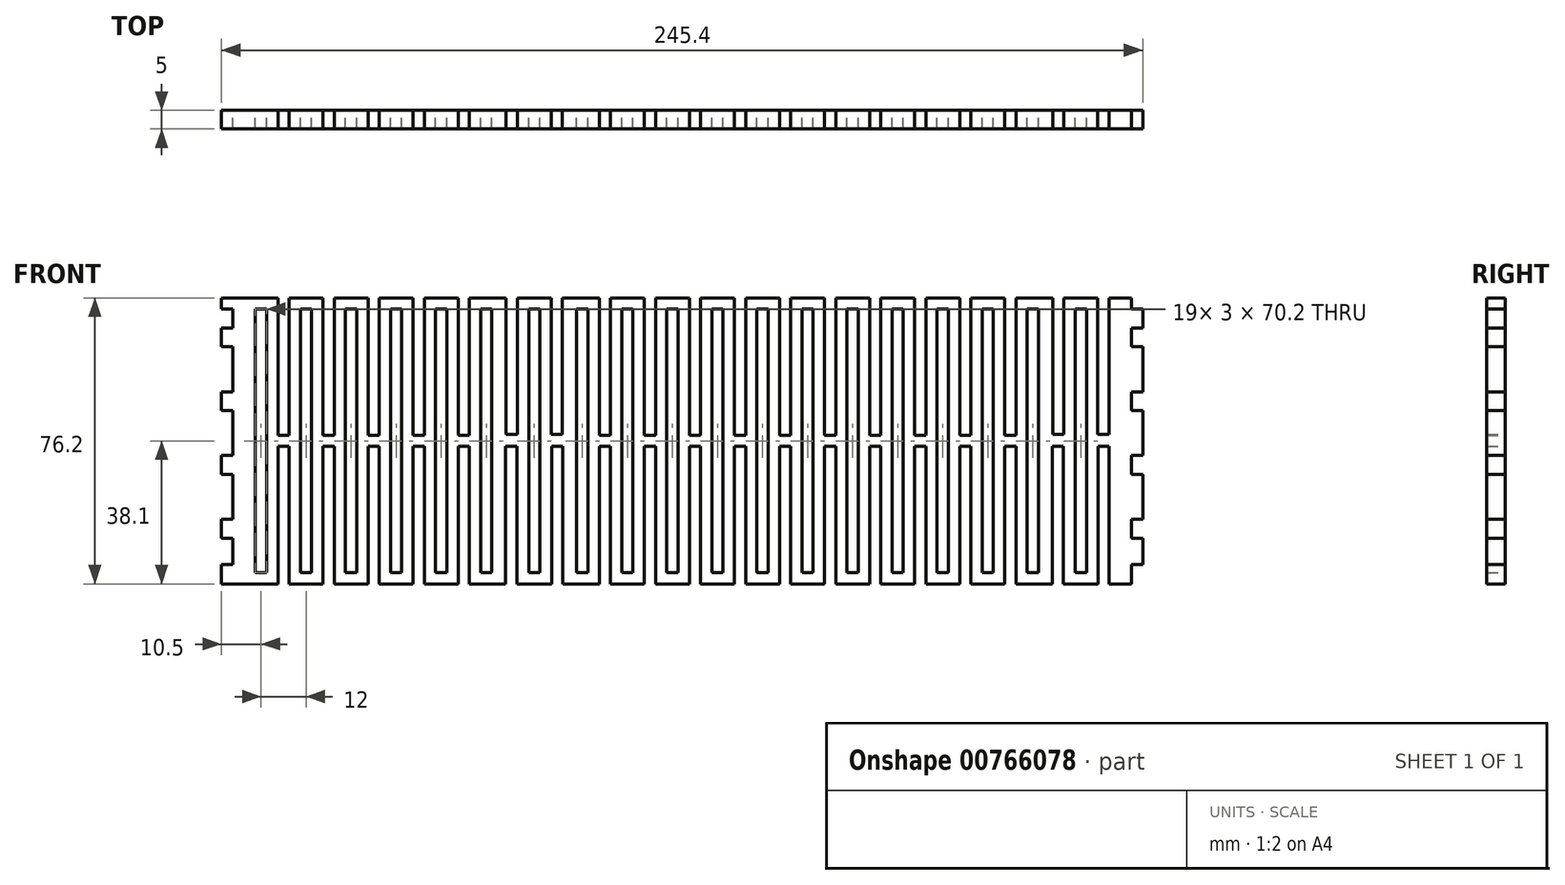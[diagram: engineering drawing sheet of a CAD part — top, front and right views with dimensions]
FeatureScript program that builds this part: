
annotation { "Feature Type Name" : "Feature", "Feature Type Description" : "" }
export const myFeature = defineFeature(function(context is Context, id is Id, definition is map)
    precondition{}
    {
        {
            var Q0;
            Q0=qCreatedBy(makeId("Front.planeOp"),FACE);
            var sketch = newSketch(context, id + "F0", { "sketchPlane" : qUnion([Q0])});
            skLineSegment(sketch, "E0.bottom", {"start": v(0, 0) * mm, "end": v(15, 0) * mm});
            skLineSegment(sketch, "E0.top", {"start": v(0, 76.2) * mm, "end": v(15, 76.2) * mm});
            skLineSegment(sketch, "E0.left", {"start": v(0, 0) * mm, "end": v(0, 5.2) * mm});
            skLineSegment(sketch, "E1.bottom", {"start": v(9, 73.2) * mm, "end": v(12, 73.2) * mm});
            skLineSegment(sketch, "E1.top", {"start": v(9, 3) * mm, "end": v(12, 3) * mm});
            skLineSegment(sketch, "E1.left", {"start": v(9, 73.2) * mm, "end": v(9, 3) * mm});
            skLineSegment(sketch, "E1.right", {"start": v(12, 73.2) * mm, "end": v(12, 3) * mm});
            skLineSegment(sketch, "E2.left", {"start": v(15, 76.2) * mm, "end": v(15, 39.6) * mm});
            skLineSegment(sketch, "E2.right", {"start": v(18, 76.2) * mm, "end": v(18, 39.6) * mm});
            skLineSegment(sketch, "E3.bottom", {"start": v(15, 36.6) * mm, "end": v(18, 36.6) * mm});
            skLineSegment(sketch, "E3.left", {"start": v(15, 36.6) * mm, "end": v(15, 0) * mm});
            skLineSegment(sketch, "E3.right", {"start": v(18, 36.6) * mm, "end": v(18, 0) * mm});
            skPoint(sketch, "E4.endSnap0", {"position": v(6, 38.1) * mm});
            skLineSegment(sketch, "E5", {"start": v(15, 39.6) * mm, "end": v(18, 39.6) * mm});
            skLineSegment(sketch, "E6.bottom", {"start": v(21, 3) * mm, "end": v(22.5, 3) * mm});
            skLineSegment(sketch, "E6.top", {"start": v(21, 73.2) * mm, "end": v(22.5, 73.2) * mm});
            skLineSegment(sketch, "E6.left", {"start": v(21, 3) * mm, "end": v(21, 73.2) * mm});
            skLineSegment(sketch, "E7.MirrorCS", {"start": v(24, 3) * mm, "end": v(24, 73.2) * mm});
            skLineSegment(sketch, "E8.MirrorCS", {"start": v(27, 76.2) * mm, "end": v(27, 39.6) * mm});
            skLineSegment(sketch, "E9.MirrorCS", {"start": v(30, 76.2) * mm, "end": v(30, 39.6) * mm});
            skLineSegment(sketch, "E10.MirrorCS", {"start": v(30, 39.6) * mm, "end": v(27, 39.6) * mm});
            skLineSegment(sketch, "E11.MirrorCS", {"start": v(30, 36.6) * mm, "end": v(27, 36.6) * mm});
            skLineSegment(sketch, "E12.MirrorCS", {"start": v(27, 36.6) * mm, "end": v(27, 0) * mm});
            skLineSegment(sketch, "E13.MirrorCS", {"start": v(30, 36.6) * mm, "end": v(30, 0) * mm});
            skLineSegment(sketch, "E14.MirrorCS", {"start": v(33, 73.2) * mm, "end": v(33, 3) * mm});
            skLineSegment(sketch, "E15.MirrorCS", {"start": v(36, 73.2) * mm, "end": v(33, 73.2) * mm});
            skLineSegment(sketch, "E16.MirrorCS", {"start": v(36, 73.2) * mm, "end": v(36, 3) * mm});
            skLineSegment(sketch, "E17.MirrorCS", {"start": v(36, 3) * mm, "end": v(33, 3) * mm});
            skLineSegment(sketch, "E18.MirrorCS", {"start": v(24, 3) * mm, "end": v(22.5, 3) * mm});
            skLineSegment(sketch, "E19", {"start": v(22.5, 73.2) * mm, "end": v(24, 73.2) * mm});
            skLineSegment(sketch, "E20.trimOffspring", {"start": v(18, 76.2) * mm, "end": v(27, 76.2) * mm});
            skLineSegment(sketch, "E21.trimOffspring", {"start": v(30, 76.2) * mm, "end": v(39, 76.2) * mm});
            skLineSegment(sketch, "E22.trimOffspring", {"start": v(30, 0) * mm, "end": v(39, 0) * mm});
            skLineSegment(sketch, "E23.trimOffspring", {"start": v(18, 0) * mm, "end": v(27, 0) * mm});
            skLineSegment(sketch, "E24", {"start": v(39, 76.2) * mm, "end": v(39, 39.6) * mm});
            skLineSegment(sketch, "E25", {"start": v(39, 39.6) * mm, "end": v(40.5, 39.6) * mm});
            skLineSegment(sketch, "E26.bottom", {"start": v(39, 36.6) * mm, "end": v(40.5, 36.6) * mm});
            skLineSegment(sketch, "E26.left", {"start": v(39, 36.6) * mm, "end": v(39, 3) * mm});
            skLineSegment(sketch, "E27.MirrorCS", {"start": v(42, 76.2) * mm, "end": v(42, 39.6) * mm});
            skLineSegment(sketch, "E28.MirrorCS", {"start": v(45, 73.2) * mm, "end": v(45, 3) * mm});
            skLineSegment(sketch, "E29.MirrorCS", {"start": v(48, 73.2) * mm, "end": v(48, 3) * mm});
            skLineSegment(sketch, "E30.MirrorCS", {"start": v(51, 76.2) * mm, "end": v(51, 39.6) * mm});
            skLineSegment(sketch, "E31.MirrorCS", {"start": v(54, 76.2) * mm, "end": v(54, 39.6) * mm});
            skLineSegment(sketch, "E32.MirrorCS", {"start": v(57, 3) * mm, "end": v(57, 73.2) * mm});
            skLineSegment(sketch, "E33.MirrorCS", {"start": v(60, 3) * mm, "end": v(60, 73.2) * mm});
            skLineSegment(sketch, "E34.MirrorCS", {"start": v(63, 76.2) * mm, "end": v(63, 39.6) * mm});
            skLineSegment(sketch, "E35.MirrorCS", {"start": v(66, 76.2) * mm, "end": v(66, 39.6) * mm});
            skLineSegment(sketch, "E36.MirrorCS", {"start": v(69, 73.2) * mm, "end": v(69, 3) * mm});
            skLineSegment(sketch, "E37.MirrorCS", {"start": v(51, 36.6) * mm, "end": v(51, 0) * mm});
            skLineSegment(sketch, "E38.MirrorCS", {"start": v(54, 36.6) * mm, "end": v(54, 0) * mm});
            skLineSegment(sketch, "E39.MirrorCS", {"start": v(63, 36.6) * mm, "end": v(63, 0) * mm});
            skLineSegment(sketch, "E40.MirrorCS", {"start": v(66, 36.6) * mm, "end": v(66, 0) * mm});
            skLineSegment(sketch, "E41.MirrorCS", {"start": v(72, 73.2) * mm, "end": v(72, 3) * mm});
            skLineSegment(sketch, "E42.MirrorCS", {"start": v(42, 36.6) * mm, "end": v(42, 3) * mm});
            skLineSegment(sketch, "E43.MirrorCS", {"start": v(45, 3) * mm, "end": v(48, 3) * mm});
            skLineSegment(sketch, "E44.MirrorCS", {"start": v(57, 3) * mm, "end": v(58.5, 3) * mm});
            skLineSegment(sketch, "E45.MirrorCS", {"start": v(60, 3) * mm, "end": v(58.5, 3) * mm});
            skLineSegment(sketch, "E46.MirrorCS", {"start": v(72, 3) * mm, "end": v(69, 3) * mm});
            skLineSegment(sketch, "E47.MirrorCS", {"start": v(51, 36.6) * mm, "end": v(54, 36.6) * mm});
            skLineSegment(sketch, "E48.MirrorCS", {"start": v(66, 39.6) * mm, "end": v(63, 39.6) * mm});
            skLineSegment(sketch, "E49.MirrorCS", {"start": v(51, 39.6) * mm, "end": v(54, 39.6) * mm});
            skLineSegment(sketch, "E50.MirrorCS", {"start": v(66, 36.6) * mm, "end": v(63, 36.6) * mm});
            skLineSegment(sketch, "E51.MirrorCS", {"start": v(42, 36.6) * mm, "end": v(40.5, 36.6) * mm});
            skLineSegment(sketch, "E52.MirrorCS", {"start": v(45, 73.2) * mm, "end": v(48, 73.2) * mm});
            skLineSegment(sketch, "E53.MirrorCS", {"start": v(58.5, 73.2) * mm, "end": v(57, 73.2) * mm});
            skLineSegment(sketch, "E54.MirrorCS", {"start": v(60, 73.2) * mm, "end": v(58.5, 73.2) * mm});
            skLineSegment(sketch, "E55.MirrorCS", {"start": v(72, 73.2) * mm, "end": v(69, 73.2) * mm});
            skLineSegment(sketch, "E56.trimOffspring", {"start": v(42, 76.2) * mm, "end": v(51, 76.2) * mm});
            skLineSegment(sketch, "E57", {"start": v(40.5, 39.6) * mm, "end": v(42, 39.6) * mm});
            skLineSegment(sketch, "E58", {"start": v(39, 3) * mm, "end": v(39, 0) * mm});
            skLineSegment(sketch, "E59", {"start": v(42, 0) * mm, "end": v(42, 3) * mm});
            skLineSegment(sketch, "E60.trimOffspring", {"start": v(42, 0) * mm, "end": v(51, 0) * mm});
            skLineSegment(sketch, "E61.trimOffspring", {"start": v(54, 0) * mm, "end": v(63, 0) * mm});
            skLineSegment(sketch, "E62.trimOffspring", {"start": v(66, 0) * mm, "end": v(75.68, 0) * mm});
            skLineSegment(sketch, "E63.trimOffspring", {"start": v(54, 76.2) * mm, "end": v(63, 76.2) * mm});
            skLineSegment(sketch, "E64.trimOffspring", {"start": v(66, 76.2) * mm, "end": v(75.8, 76.2) * mm});
            skLineSegment(sketch, "E65.top", {"start": v(75.8, 39.81) * mm, "end": v(78.8, 39.81) * mm});
            skLineSegment(sketch, "E65.left", {"start": v(75.8, 76.2) * mm, "end": v(75.8, 39.81) * mm});
            skLineSegment(sketch, "E65.right", {"start": v(78.8, 76.2) * mm, "end": v(78.8, 39.81) * mm});
            skLineSegment(sketch, "E66.bottom", {"start": v(75.68, 36.6) * mm, "end": v(78.66, 36.6) * mm});
            skLineSegment(sketch, "E66.left", {"start": v(75.68, 36.6) * mm, "end": v(75.68, 0) * mm});
            skLineSegment(sketch, "E66.right", {"start": v(78.66, 36.6) * mm, "end": v(78.66, 0) * mm});
            skLineSegment(sketch, "E67.bottom", {"start": v(81.8, 73.2) * mm, "end": v(83.3, 73.2) * mm});
            skLineSegment(sketch, "E67.top", {"start": v(81.8, 3) * mm, "end": v(83.3, 3) * mm});
            skLineSegment(sketch, "E67.left", {"start": v(81.8, 73.2) * mm, "end": v(81.8, 3) * mm});
            skPoint(sketch, "E68.orphan", {"position": v(73.83, 73.2) * mm});
            skLineSegment(sketch, "E69.MirrorCS", {"start": v(84.8, 73.2) * mm, "end": v(84.8, 3) * mm});
            skLineSegment(sketch, "E70.MirrorCS", {"start": v(87.8, 76.2) * mm, "end": v(87.8, 39.81) * mm});
            skLineSegment(sketch, "E71.MirrorCS", {"start": v(90.8, 76.2) * mm, "end": v(90.8, 39.81) * mm});
            skLineSegment(sketch, "E72.MirrorCS", {"start": v(94.6, 73.2) * mm, "end": v(94.6, 3) * mm});
            skLineSegment(sketch, "E73.MirrorCS", {"start": v(97.6, 73.2) * mm, "end": v(97.6, 3) * mm});
            skLineSegment(sketch, "E74.MirrorCS", {"start": v(100.6, 76.2) * mm, "end": v(100.6, 39.6) * mm});
            skLineSegment(sketch, "E75.MirrorCS", {"start": v(103.6, 76.2) * mm, "end": v(103.6, 39.6) * mm});
            skLineSegment(sketch, "E76.MirrorCS", {"start": v(106.6, 3) * mm, "end": v(106.6, 73.2) * mm});
            skLineSegment(sketch, "E77.MirrorCS", {"start": v(109.6, 3) * mm, "end": v(109.6, 73.2) * mm});
            skLineSegment(sketch, "E78.MirrorCS", {"start": v(112.6, 76.2) * mm, "end": v(112.6, 39.6) * mm});
            skLineSegment(sketch, "E79.MirrorCS", {"start": v(115.6, 76.2) * mm, "end": v(115.6, 39.6) * mm});
            skLineSegment(sketch, "E80.MirrorCS", {"start": v(118.6, 73.2) * mm, "end": v(118.6, 3) * mm});
            skLineSegment(sketch, "E81.MirrorCS", {"start": v(121.6, 73.2) * mm, "end": v(121.6, 3) * mm});
            skLineSegment(sketch, "E82.MirrorCS", {"start": v(124.6, 76.2) * mm, "end": v(124.6, 39.6) * mm});
            skLineSegment(sketch, "E83.MirrorCS", {"start": v(127.6, 76.2) * mm, "end": v(127.6, 39.6) * mm});
            skLineSegment(sketch, "E84.MirrorCS", {"start": v(130.6, 73.2) * mm, "end": v(130.6, 3) * mm});
            skLineSegment(sketch, "E85.MirrorCS", {"start": v(133.6, 73.2) * mm, "end": v(133.6, 3) * mm});
            skLineSegment(sketch, "E86.MirrorCS", {"start": v(136.6, 76.2) * mm, "end": v(136.6, 39.6) * mm});
            skLineSegment(sketch, "E87.MirrorCS", {"start": v(139.6, 76.2) * mm, "end": v(139.6, 39.6) * mm});
            skLineSegment(sketch, "E88.MirrorCS", {"start": v(142.6, 3) * mm, "end": v(142.6, 73.2) * mm});
            skLineSegment(sketch, "E89.MirrorCS", {"start": v(148.6, 76.2) * mm, "end": v(148.6, 39.6) * mm});
            skLineSegment(sketch, "E90.MirrorCS", {"start": v(151.6, 76.2) * mm, "end": v(151.6, 39.6) * mm});
            skLineSegment(sketch, "E91.MirrorCS", {"start": v(94.6, 73.2) * mm, "end": v(97.6, 73.2) * mm});
            skLineSegment(sketch, "E92.MirrorCS", {"start": v(84.8, 73.2) * mm, "end": v(83.3, 73.2) * mm});
            skLineSegment(sketch, "E93.MirrorCS", {"start": v(121.6, 73.2) * mm, "end": v(118.6, 73.2) * mm});
            skLineSegment(sketch, "E94.MirrorCS", {"start": v(108.1, 73.2) * mm, "end": v(109.6, 73.2) * mm});
            skLineSegment(sketch, "E95.MirrorCS", {"start": v(106.6, 73.2) * mm, "end": v(108.1, 73.2) * mm});
            skLineSegment(sketch, "E96.MirrorCS", {"start": v(130.6, 73.2) * mm, "end": v(133.6, 73.2) * mm});
            skLineSegment(sketch, "E97.MirrorCS", {"start": v(144.1, 73.2) * mm, "end": v(142.6, 73.2) * mm});
            skLineSegment(sketch, "E98.MirrorCS", {"start": v(145.6, 73.2) * mm, "end": v(144.1, 73.2) * mm});
            skLineSegment(sketch, "E99.MirrorCS", {"start": v(156.1, 73.2) * mm, "end": v(154.6, 73.2) * mm});
            skLineSegment(sketch, "E100.MirrorCS", {"start": v(90.8, 39.81) * mm, "end": v(87.8, 39.81) * mm});
            skLineSegment(sketch, "E101.MirrorCS", {"start": v(100.6, 39.6) * mm, "end": v(103.6, 39.6) * mm});
            skLineSegment(sketch, "E102.MirrorCS", {"start": v(115.6, 39.6) * mm, "end": v(112.6, 39.6) * mm});
            skLineSegment(sketch, "E103.MirrorCS", {"start": v(126.1, 39.6) * mm, "end": v(124.6, 39.6) * mm});
            skLineSegment(sketch, "E104.MirrorCS", {"start": v(127.6, 39.6) * mm, "end": v(126.1, 39.6) * mm});
            skLineSegment(sketch, "E105.MirrorCS", {"start": v(136.6, 39.6) * mm, "end": v(139.6, 39.6) * mm});
            skLineSegment(sketch, "E106.MirrorCS", {"start": v(151.6, 39.6) * mm, "end": v(148.6, 39.6) * mm});
            skLineSegment(sketch, "E107.MirrorCS", {"start": v(151.6, 36.6) * mm, "end": v(148.6, 36.6) * mm});
            skLineSegment(sketch, "E108.MirrorCS", {"start": v(136.6, 36.6) * mm, "end": v(139.6, 36.6) * mm});
            skLineSegment(sketch, "E109.MirrorCS", {"start": v(124.6, 36.6) * mm, "end": v(126.1, 36.6) * mm});
            skLineSegment(sketch, "E110.MirrorCS", {"start": v(115.6, 36.6) * mm, "end": v(112.6, 36.6) * mm});
            skLineSegment(sketch, "E111.MirrorCS", {"start": v(100.6, 36.6) * mm, "end": v(103.6, 36.6) * mm});
            skLineSegment(sketch, "E112.MirrorCS", {"start": v(87.94, 36.6) * mm, "end": v(87.94, 0) * mm});
            skLineSegment(sketch, "E113.MirrorCS", {"start": v(90.92, 36.6) * mm, "end": v(90.92, 0) * mm});
            skLineSegment(sketch, "E114.MirrorCS", {"start": v(100.6, 36.6) * mm, "end": v(100.6, 0) * mm});
            skLineSegment(sketch, "E115.MirrorCS", {"start": v(103.6, 36.6) * mm, "end": v(103.6, 0) * mm});
            skLineSegment(sketch, "E116.MirrorCS", {"start": v(112.6, 36.6) * mm, "end": v(112.6, 0) * mm});
            skLineSegment(sketch, "E117.MirrorCS", {"start": v(115.6, 36.6) * mm, "end": v(115.6, 0) * mm});
            skLineSegment(sketch, "E118.MirrorCS", {"start": v(124.6, 36.6) * mm, "end": v(124.6, 3) * mm});
            skLineSegment(sketch, "E119.MirrorCS", {"start": v(127.6, 36.6) * mm, "end": v(127.6, 3) * mm});
            skLineSegment(sketch, "E120.MirrorCS", {"start": v(124.6, 0) * mm, "end": v(124.6, 3) * mm});
            skLineSegment(sketch, "E121.MirrorCS", {"start": v(127.6, 3) * mm, "end": v(127.6, 0) * mm});
            skLineSegment(sketch, "E122.MirrorCS", {"start": v(136.6, 36.6) * mm, "end": v(136.6, 0) * mm});
            skLineSegment(sketch, "E123.MirrorCS", {"start": v(139.6, 36.6) * mm, "end": v(139.6, 0) * mm});
            skLineSegment(sketch, "E124.MirrorCS", {"start": v(84.8, 3) * mm, "end": v(83.3, 3) * mm});
            skLineSegment(sketch, "E125.MirrorCS", {"start": v(94.6, 3) * mm, "end": v(97.6, 3) * mm});
            skLineSegment(sketch, "E126.MirrorCS", {"start": v(106.6, 3) * mm, "end": v(108.1, 3) * mm});
            skLineSegment(sketch, "E127.MirrorCS", {"start": v(109.6, 3) * mm, "end": v(108.1, 3) * mm});
            skLineSegment(sketch, "E128.MirrorCS", {"start": v(121.6, 3) * mm, "end": v(118.6, 3) * mm});
            skLineSegment(sketch, "E129.MirrorCS", {"start": v(130.6, 3) * mm, "end": v(133.6, 3) * mm});
            skLineSegment(sketch, "E130.MirrorCS", {"start": v(142.6, 3) * mm, "end": v(144.1, 3) * mm});
            skLineSegment(sketch, "E131.MirrorCS", {"start": v(154.6, 73.2) * mm, "end": v(154.6, 3) * mm});
            skLineSegment(sketch, "E132.MirrorCS", {"start": v(145.6, 3) * mm, "end": v(145.6, 73.2) * mm});
            skLineSegment(sketch, "E133.MirrorCS", {"start": v(151.6, 36.6) * mm, "end": v(151.6, 0) * mm});
            skLineSegment(sketch, "E134.MirrorCS", {"start": v(148.6, 36.6) * mm, "end": v(148.6, 0) * mm});
            skLineSegment(sketch, "E135.trimOffspring", {"start": v(103.6, 76.2) * mm, "end": v(112.6, 76.2) * mm});
            skLineSegment(sketch, "E136.trimOffspring", {"start": v(90.8, 76.2) * mm, "end": v(100.6, 76.2) * mm});
            skLineSegment(sketch, "E137.trimOffspring", {"start": v(115.6, 76.2) * mm, "end": v(124.6, 76.2) * mm});
            skLineSegment(sketch, "E138.trimOffspring", {"start": v(127.6, 76.2) * mm, "end": v(136.6, 76.2) * mm});
            skLineSegment(sketch, "E139.trimOffspring", {"start": v(139.6, 76.2) * mm, "end": v(148.6, 76.2) * mm});
            skLineSegment(sketch, "E140.trimOffspring", {"start": v(151.6, 76.2) * mm, "end": v(160.6, 76.2) * mm});
            skLineSegment(sketch, "E141.trimOffspring", {"start": v(151.6, 0) * mm, "end": v(160.6, 0) * mm});
            skLineSegment(sketch, "E142.trimOffspring", {"start": v(139.6, 0) * mm, "end": v(148.6, 0) * mm});
            skLineSegment(sketch, "E143.trimOffspring", {"start": v(127.6, 0) * mm, "end": v(136.6, 0) * mm});
            skLineSegment(sketch, "E144.trimOffspring", {"start": v(115.6, 0) * mm, "end": v(124.6, 0) * mm});
            skLineSegment(sketch, "E145.trimOffspring", {"start": v(103.6, 0) * mm, "end": v(112.6, 0) * mm});
            skLineSegment(sketch, "E146.trimOffspring", {"start": v(90.92, 0) * mm, "end": v(100.6, 0) * mm});
            skLineSegment(sketch, "E147", {"start": v(144.1, 3) * mm, "end": v(145.6, 3) * mm});
            skLineSegment(sketch, "E148", {"start": v(154.6, 3) * mm, "end": v(156.1, 3) * mm});
            skLineSegment(sketch, "E149", {"start": v(87.94, 36.6) * mm, "end": v(90.92, 36.6) * mm});
            skLineSegment(sketch, "E150", {"start": v(126.1, 36.6) * mm, "end": v(127.6, 36.6) * mm});
            skPoint(sketch, "E151.end.orphan", {"position": v(157.6, 0) * mm});
            skPoint(sketch, "E152.orphan", {"position": v(157.6, 3) * mm});
            skLineSegment(sketch, "E153.MirrorCS", {"start": v(157.6, 73.2) * mm, "end": v(157.6, 3) * mm});
            skLineSegment(sketch, "E154.MirrorCS", {"start": v(160.6, 76.2) * mm, "end": v(160.6, 39.6) * mm});
            skLineSegment(sketch, "E155.MirrorCS", {"start": v(163.6, 76.2) * mm, "end": v(163.6, 39.6) * mm});
            skLineSegment(sketch, "E156.MirrorCS", {"start": v(166.6, 3) * mm, "end": v(166.6, 73.2) * mm});
            skLineSegment(sketch, "E157.MirrorCS", {"start": v(169.6, 3) * mm, "end": v(169.6, 73.2) * mm});
            skLineSegment(sketch, "E158.MirrorCS", {"start": v(172.6, 76.2) * mm, "end": v(172.6, 39.6) * mm});
            skLineSegment(sketch, "E159.MirrorCS", {"start": v(175.6, 76.2) * mm, "end": v(175.6, 39.6) * mm});
            skLineSegment(sketch, "E160.MirrorCS", {"start": v(178.6, 73.2) * mm, "end": v(178.6, 3) * mm});
            skLineSegment(sketch, "E161.MirrorCS", {"start": v(181.6, 73.2) * mm, "end": v(181.6, 3) * mm});
            skLineSegment(sketch, "E162.MirrorCS", {"start": v(184.6, 76.2) * mm, "end": v(184.6, 39.6) * mm});
            skLineSegment(sketch, "E163.MirrorCS", {"start": v(187.6, 76.2) * mm, "end": v(187.6, 39.6) * mm});
            skLineSegment(sketch, "E164.MirrorCS", {"start": v(190.6, 73.2) * mm, "end": v(190.6, 3) * mm});
            skLineSegment(sketch, "E165.MirrorCS", {"start": v(193.6, 73.2) * mm, "end": v(193.6, 3) * mm});
            skLineSegment(sketch, "E166.MirrorCS", {"start": v(190.6, 73.2) * mm, "end": v(193.6, 73.2) * mm});
            skLineSegment(sketch, "E167.MirrorCS", {"start": v(199.6, 76.2) * mm, "end": v(199.6, 39.6) * mm});
            skLineSegment(sketch, "E168.MirrorCS", {"start": v(202.6, 3) * mm, "end": v(202.6, 73.2) * mm});
            skLineSegment(sketch, "E169.MirrorCS", {"start": v(205.6, 3) * mm, "end": v(205.6, 73.2) * mm});
            skLineSegment(sketch, "E170.MirrorCS", {"start": v(208.6, 76.2) * mm, "end": v(208.6, 39.6) * mm});
            skLineSegment(sketch, "E171.MirrorCS", {"start": v(211.6, 76.2) * mm, "end": v(211.6, 39.6) * mm});
            skLineSegment(sketch, "E172.MirrorCS", {"start": v(214.6, 73.2) * mm, "end": v(214.6, 3) * mm});
            skLineSegment(sketch, "E173.MirrorCS", {"start": v(217.6, 73.2) * mm, "end": v(217.6, 3) * mm});
            skLineSegment(sketch, "E174.MirrorCS", {"start": v(157.6, 3) * mm, "end": v(156.1, 3) * mm});
            skLineSegment(sketch, "E175.MirrorCS", {"start": v(168.1, 3) * mm, "end": v(166.6, 3) * mm});
            skLineSegment(sketch, "E176.MirrorCS", {"start": v(169.6, 3) * mm, "end": v(168.1, 3) * mm});
            skLineSegment(sketch, "E177.MirrorCS", {"start": v(172.6, 36.6) * mm, "end": v(172.6, 0) * mm});
            skLineSegment(sketch, "E178.MirrorCS", {"start": v(175.6, 36.6) * mm, "end": v(175.6, 0) * mm});
            skLineSegment(sketch, "E179.MirrorCS", {"start": v(181.6, 3) * mm, "end": v(178.6, 3) * mm});
            skLineSegment(sketch, "E180.MirrorCS", {"start": v(184.6, 0) * mm, "end": v(175.6, 0) * mm});
            skLineSegment(sketch, "E181.MirrorCS", {"start": v(190.6, 3) * mm, "end": v(193.6, 3) * mm});
            skLineSegment(sketch, "E182.MirrorCS", {"start": v(184.6, 36.6) * mm, "end": v(184.6, 3) * mm});
            skLineSegment(sketch, "E183.MirrorCS", {"start": v(187.6, 36.6) * mm, "end": v(187.6, 3) * mm});
            skLineSegment(sketch, "E184.MirrorCS", {"start": v(187.6, 0) * mm, "end": v(187.6, 3) * mm});
            skLineSegment(sketch, "E185.MirrorCS", {"start": v(184.6, 3) * mm, "end": v(184.6, 0) * mm});
            skLineSegment(sketch, "E186.MirrorCS", {"start": v(196.6, 36.6) * mm, "end": v(196.6, 0) * mm});
            skLineSegment(sketch, "E187.MirrorCS", {"start": v(199.6, 36.6) * mm, "end": v(199.6, 0) * mm});
            skLineSegment(sketch, "E188.MirrorCS", {"start": v(202.6, 3) * mm, "end": v(204.1, 3) * mm});
            skLineSegment(sketch, "E189.MirrorCS", {"start": v(205.6, 3) * mm, "end": v(204.1, 3) * mm});
            skLineSegment(sketch, "E190.MirrorCS", {"start": v(217.6, 3) * mm, "end": v(214.6, 3) * mm});
            skLineSegment(sketch, "E191.MirrorCS", {"start": v(211.6, 36.6) * mm, "end": v(211.6, 0) * mm});
            skLineSegment(sketch, "E192.MirrorCS", {"start": v(221.28, 36.6) * mm, "end": v(221.28, 0) * mm});
            skLineSegment(sketch, "E193.MirrorCS", {"start": v(227.4, 73.2) * mm, "end": v(227.4, 3) * mm});
            skLineSegment(sketch, "E194.MirrorCS", {"start": v(160.6, 36.6) * mm, "end": v(160.6, 0) * mm});
            skLineSegment(sketch, "E195.MirrorCS", {"start": v(175.6, 39.6) * mm, "end": v(172.6, 39.6) * mm});
            skLineSegment(sketch, "E196.MirrorCS", {"start": v(184.6, 39.6) * mm, "end": v(186.1, 39.6) * mm});
            skLineSegment(sketch, "E197.MirrorCS", {"start": v(186.1, 39.6) * mm, "end": v(187.6, 39.6) * mm});
            skLineSegment(sketch, "E198.MirrorCS", {"start": v(196.6, 39.6) * mm, "end": v(199.6, 39.6) * mm});
            skLineSegment(sketch, "E199.MirrorCS", {"start": v(211.6, 39.6) * mm, "end": v(208.6, 39.6) * mm});
            skLineSegment(sketch, "E200.MirrorCS", {"start": v(163.6, 36.6) * mm, "end": v(163.6, 0) * mm});
            skLineSegment(sketch, "E201.MirrorCS", {"start": v(160.6, 36.6) * mm, "end": v(163.6, 36.6) * mm});
            skLineSegment(sketch, "E202.MirrorCS", {"start": v(175.6, 36.6) * mm, "end": v(172.6, 36.6) * mm});
            skLineSegment(sketch, "E203.MirrorCS", {"start": v(186.1, 36.6) * mm, "end": v(184.6, 36.6) * mm});
            skLineSegment(sketch, "E204.MirrorCS", {"start": v(187.6, 36.6) * mm, "end": v(186.1, 36.6) * mm});
            skLineSegment(sketch, "E205.MirrorCS", {"start": v(196.6, 36.6) * mm, "end": v(199.6, 36.6) * mm});
            skLineSegment(sketch, "E206.MirrorCS", {"start": v(211.6, 36.6) * mm, "end": v(208.6, 36.6) * mm});
            skLineSegment(sketch, "E207.MirrorCS", {"start": v(233.54, 36.6) * mm, "end": v(233.54, 0) * mm});
            skLineSegment(sketch, "E208.MirrorCS", {"start": v(236.52, 36.6) * mm, "end": v(236.52, 0) * mm});
            skLineSegment(sketch, "E209.MirrorCS", {"start": v(208.6, 36.6) * mm, "end": v(208.6, 0) * mm});
            skLineSegment(sketch, "E210.MirrorCS", {"start": v(196.6, 76.2) * mm, "end": v(196.6, 39.6) * mm});
            skLineSegment(sketch, "E211.MirrorCS", {"start": v(236.4, 76.2) * mm, "end": v(236.4, 39.81) * mm});
            skLineSegment(sketch, "E212.MirrorCS", {"start": v(233.4, 76.2) * mm, "end": v(233.4, 39.81) * mm});
            skLineSegment(sketch, "E213.MirrorCS", {"start": v(230.4, 73.2) * mm, "end": v(230.4, 3) * mm});
            skLineSegment(sketch, "E214.MirrorCS", {"start": v(224.4, 76.2) * mm, "end": v(224.4, 39.81) * mm});
            skLineSegment(sketch, "E215.MirrorCS", {"start": v(221.4, 76.2) * mm, "end": v(221.4, 39.81) * mm});
            skLineSegment(sketch, "E216.MirrorCS", {"start": v(224.26, 36.6) * mm, "end": v(224.26, 0) * mm});
            skLineSegment(sketch, "E217.trimOffspring", {"start": v(163.6, 0) * mm, "end": v(172.6, 0) * mm});
            skLineSegment(sketch, "E218.trimOffspring", {"start": v(175.6, 0) * mm, "end": v(184.6, 0) * mm});
            skLineSegment(sketch, "E219", {"start": v(157.6, 73.2) * mm, "end": v(156.1, 73.2) * mm});
            skLineSegment(sketch, "E220", {"start": v(166.6, 73.2) * mm, "end": v(169.6, 73.2) * mm});
            skLineSegment(sketch, "E221", {"start": v(178.6, 73.2) * mm, "end": v(181.6, 73.2) * mm});
            skLineSegment(sketch, "E222", {"start": v(202.6, 73.2) * mm, "end": v(205.6, 73.2) * mm});
            skLineSegment(sketch, "E223", {"start": v(160.6, 39.6) * mm, "end": v(163.6, 39.6) * mm});
            skLineSegment(sketch, "E224", {"start": v(221.4, 39.81) * mm, "end": v(224.4, 39.81) * mm});
            skLineSegment(sketch, "E225", {"start": v(221.28, 36.6) * mm, "end": v(224.26, 36.6) * mm});
            skLineSegment(sketch, "E226", {"start": v(214.6, 73.2) * mm, "end": v(217.6, 73.2) * mm});
            skLineSegment(sketch, "E227", {"start": v(227.4, 73.2) * mm, "end": v(230.4, 73.2) * mm});
            skLineSegment(sketch, "E228", {"start": v(233.4, 39.81) * mm, "end": v(236.4, 39.81) * mm});
            skLineSegment(sketch, "E229", {"start": v(233.54, 36.6) * mm, "end": v(236.52, 36.6) * mm});
            skLineSegment(sketch, "E230", {"start": v(227.4, 3) * mm, "end": v(230.4, 3) * mm});
            skLineSegment(sketch, "E231.trimOffspring", {"start": v(163.6, 76.2) * mm, "end": v(172.6, 76.2) * mm});
            skLineSegment(sketch, "E232.trimOffspring", {"start": v(175.6, 76.2) * mm, "end": v(184.6, 76.2) * mm});
            skLineSegment(sketch, "E233.trimOffspring", {"start": v(187.6, 76.2) * mm, "end": v(196.6, 76.2) * mm});
            skLineSegment(sketch, "E234.trimOffspring", {"start": v(199.6, 76.2) * mm, "end": v(208.6, 76.2) * mm});
            skLineSegment(sketch, "E235.trimOffspring", {"start": v(187.6, 0) * mm, "end": v(196.6, 0) * mm});
            skLineSegment(sketch, "E236.trimOffspring", {"start": v(211.6, 0) * mm, "end": v(221.28, 0) * mm});
            skLineSegment(sketch, "E237", {"start": v(199.6, 0) * mm, "end": v(208.6, 0) * mm});
            skLineSegment(sketch, "E238.trimOffspring", {"start": v(224.26, 0) * mm, "end": v(233.54, 0) * mm});
            skLineSegment(sketch, "E239.trimOffspring", {"start": v(211.6, 76.2) * mm, "end": v(221.4, 76.2) * mm});
            skLineSegment(sketch, "E240", {"start": v(224.4, 76.2) * mm, "end": v(233.4, 76.2) * mm});
            skPoint(sketch, "E241.end.orphan", {"position": v(273.2, 0) * mm});
            skPoint(sketch, "E242.end.orphan", {"position": v(238.7, 73.2) * mm});
            skPoint(sketch, "E242.start.orphan", {"position": v(241.4, 73.2) * mm});
            skLineSegment(sketch, "E243.bottom", {"start": v(236.4, 76.2) * mm, "end": v(239.4, 76.2) * mm});
            skLineSegment(sketch, "E243.top", {"start": v(236.4, 0) * mm, "end": v(239.4, 0) * mm});
            skLineSegment(sketch, "E244.trimOffspring", {"start": v(236.4, 36.6) * mm, "end": v(236.4, 0) * mm});
            skLineSegment(sketch, "E245.bottom", {"start": v(239.4, 76.2) * mm, "end": v(242.4, 76.2) * mm});
            skLineSegment(sketch, "E245.top", {"start": v(239.4, 0) * mm, "end": v(242.4, 0) * mm});
            skLineSegment(sketch, "E245.right", {"start": v(245.4, 73.2) * mm, "end": v(245.4, 68.2) * mm});
            skLineSegment(sketch, "E246.bottom", {"start": v(242.4, 73.2) * mm, "end": v(245.4, 73.2) * mm});
            skLineSegment(sketch, "E246.top", {"start": v(242.4, 68.2) * mm, "end": v(245.4, 68.2) * mm});
            skLineSegment(sketch, "E247.bottom", {"start": v(242.4, 63.2) * mm, "end": v(245.4, 63.2) * mm});
            skLineSegment(sketch, "E247.top", {"start": v(242.4, 51.2) * mm, "end": v(245.4, 51.2) * mm});
            skLineSegment(sketch, "E247.right", {"start": v(245.4, 63.2) * mm, "end": v(245.4, 51.2) * mm});
            skLineSegment(sketch, "E248.bottom", {"start": v(242.4, 46.2) * mm, "end": v(245.4, 46.2) * mm});
            skLineSegment(sketch, "E248.top", {"start": v(242.4, 34.2) * mm, "end": v(245.4, 34.2) * mm});
            skLineSegment(sketch, "E248.right", {"start": v(245.4, 46.2) * mm, "end": v(245.4, 34.2) * mm});
            skLineSegment(sketch, "E249.bottom", {"start": v(245.4, 29.2) * mm, "end": v(242.4, 29.2) * mm});
            skLineSegment(sketch, "E249.top", {"start": v(245.4, 17.2) * mm, "end": v(242.4, 17.2) * mm});
            skLineSegment(sketch, "E249.left", {"start": v(245.4, 29.2) * mm, "end": v(245.4, 17.2) * mm});
            skPoint(sketch, "E250.oppositeSnap0", {"position": v(242.4, 0) * mm});
            skLineSegment(sketch, "E250.bottom", {"start": v(245.4, 12.2) * mm, "end": v(242.4, 12.2) * mm});
            skLineSegment(sketch, "E250.top", {"start": v(245.4, 5.2) * mm, "end": v(242.4, 5.2) * mm});
            skLineSegment(sketch, "E250.left", {"start": v(245.4, 12.2) * mm, "end": v(245.4, 5.2) * mm});
            skLineSegment(sketch, "E251", {"start": v(3, 73.2) * mm, "end": v(3, 68.2) * mm});
            skLineSegment(sketch, "E252", {"start": v(3, 38.1) * mm, "end": v(3, 34.2) * mm});
            skLineSegment(sketch, "E253", {"start": v(0, 73.2) * mm, "end": v(3, 73.2) * mm});
            skLineSegment(sketch, "E254", {"start": v(0, 68.2) * mm, "end": v(3, 68.2) * mm});
            skLineSegment(sketch, "E255.trimOffspring", {"start": v(0, 73.2) * mm, "end": v(0, 76.2) * mm});
            skLineSegment(sketch, "E256", {"start": v(0, 63.2) * mm, "end": v(3, 63.2) * mm});
            skLineSegment(sketch, "E257.top", {"start": v(0, 51.2) * mm, "end": v(3, 51.2) * mm});
            skLineSegment(sketch, "E257.right", {"start": v(3, 63.2) * mm, "end": v(3, 51.2) * mm});
            skLineSegment(sketch, "E258", {"start": v(0, 46.2) * mm, "end": v(3, 46.2) * mm});
            skLineSegment(sketch, "E259", {"start": v(0, 34.2) * mm, "end": v(3, 34.2) * mm});
            skLineSegment(sketch, "E260", {"start": v(0, 29.2) * mm, "end": v(3, 29.2) * mm});
            skLineSegment(sketch, "E261", {"start": v(0, 17.2) * mm, "end": v(3, 17.2) * mm});
            skLineSegment(sketch, "E262", {"start": v(0, 12.2) * mm, "end": v(3, 12.2) * mm});
            skLineSegment(sketch, "E263", {"start": v(3, 12.2) * mm, "end": v(3, 5.2) * mm});
            skLineSegment(sketch, "E264", {"start": v(3, 5.2) * mm, "end": v(0, 5.2) * mm});
            skLineSegment(sketch, "E265.trimOffspring", {"start": v(0, 63.2) * mm, "end": v(0, 68.2) * mm});
            skLineSegment(sketch, "E266.trimOffspring", {"start": v(0, 46.2) * mm, "end": v(0, 51.2) * mm});
            skPoint(sketch, "E267.orphan", {"position": v(0, 38.1) * mm});
            skLineSegment(sketch, "E268.trimOffspring", {"start": v(0, 29.2) * mm, "end": v(0, 34.2) * mm});
            skLineSegment(sketch, "E269.trimOffspring", {"start": v(0, 12.2) * mm, "end": v(0, 17.2) * mm});
            skPoint(sketch, "E270.trimOffspring.end.orphan", {"position": v(196.3, 38.1) * mm});
            skLineSegment(sketch, "E271", {"start": v(242.4, 73.2) * mm, "end": v(242.4, 76.2) * mm});
            skLineSegment(sketch, "E272", {"start": v(242.4, 76.2) * mm, "end": v(242.4, 73.2) * mm});
            skLineSegment(sketch, "E273", {"start": v(242.4, 46.2) * mm, "end": v(242.4, 51.2) * mm});
            skLineSegment(sketch, "E274", {"start": v(242.4, 34.2) * mm, "end": v(242.4, 29.2) * mm});
            skLineSegment(sketch, "E275", {"start": v(242.4, 17.2) * mm, "end": v(242.4, 12.2) * mm});
            skLineSegment(sketch, "E276", {"start": v(242.4, 5.2) * mm, "end": v(242.4, 0) * mm});
            skPoint(sketch, "E277.orphan", {"position": v(245.4, 76.2) * mm});
            skPoint(sketch, "E278.orphan", {"position": v(245.4, 0) * mm});
            skLineSegment(sketch, "E279.trimOffspring", {"start": v(242.4, 68.2) * mm, "end": v(242.4, 63.2) * mm});
            skLineSegment(sketch, "E280.trimOffspring", {"start": v(3, 46.2) * mm, "end": v(3, 38.1) * mm});
            skLineSegment(sketch, "E281.trimOffspring", {"start": v(3, 29.2) * mm, "end": v(3, 17.2) * mm});
            skPoint(sketch, "E282.orphan", {"position": v(6, 0) * mm});
            skPoint(sketch, "E283.start.orphan", {"position": v(6, 76.2) * mm});
            skLineSegment(sketch, "E284.trimOffspring", {"start": v(78.66, 0) * mm, "end": v(87.94, 0) * mm});
            skLineSegment(sketch, "E285.trimOffspring", {"start": v(78.8, 76.2) * mm, "end": v(87.8, 76.2) * mm});
            skSolve(sketch);
        }
        {
            var Q0;
            Q0 = qSketchRegion(id + "F0", true);
            extrude(context, id + "F1", {"entities" : qUnion([Q0]), "depth" : 5 * mm, "offsetDistance" : 25 * mm});
        }
    });
